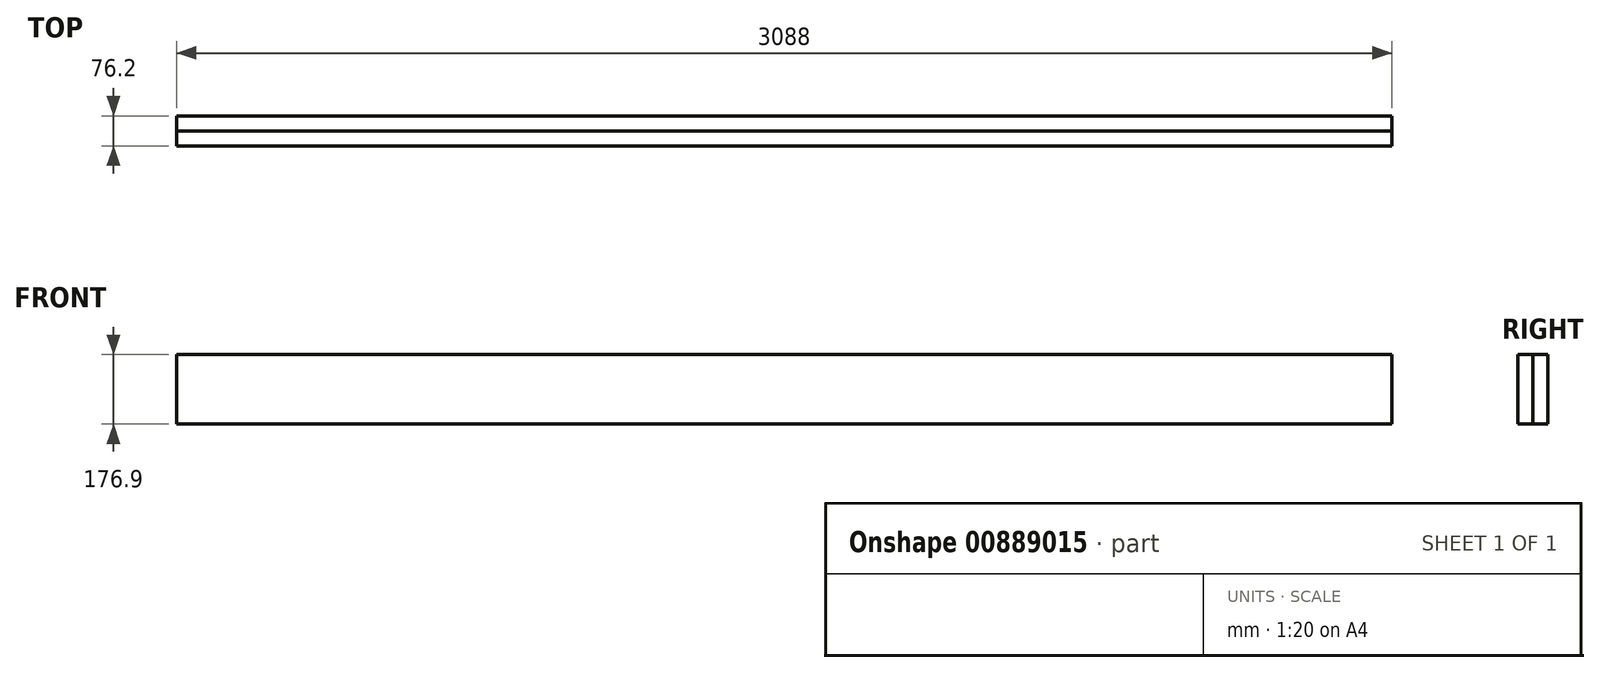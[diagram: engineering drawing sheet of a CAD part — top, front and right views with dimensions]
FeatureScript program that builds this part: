
annotation { "Feature Type Name" : "Feature", "Feature Type Description" : "" }
export const myFeature = defineFeature(function(context is Context, id is Id, definition is map)
    precondition{}
    {
        {
            var Q0;
            Q0=qCreatedBy(makeId("Top.planeOp"),FACE);
            var sketch = newSketch(context, id + "F0", { "sketchPlane" : qUnion([Q0])});
            skLineSegment(sketch, "E0.bottom", {"start": v(-1544, -38.1) * mm, "end": v(1544, -38.1) * mm});
            skLineSegment(sketch, "E0.top", {"start": v(-1544, 38.1) * mm, "end": v(1544, 38.1) * mm});
            skLineSegment(sketch, "E0.left", {"start": v(-1544, -38.1) * mm, "end": v(-1544, 38.1) * mm});
            skLineSegment(sketch, "E0.right", {"start": v(1544, -38.1) * mm, "end": v(1544, 38.1) * mm});
            skPoint(sketch, "E0.middle", {"position": v(0, 0) * mm});
            skLineSegment(sketch, "E1", {"start": v(-1544, 0) * mm, "end": v(1544, 0) * mm});
            skSolve(sketch);
        }
        {
            var Q0;
            {var subQ0=sQuery(id+"F0.wireOp",EDGE,"E0.top");Q0=makeQuery(id+"F0.imprint","IMPRINT",FACE,{"disambiguationData":[TD([[makeQuery(id+"F0.imprint","IMPRINT",EDGE,{"derivedFrom":subQ0}),-1.0]])]});}
            extrude(context, id + "F1", {"entities" : qUnion([Q0]), "endBound" : BoundingType.SYMMETRIC, "depth" : 176.9 * mm, "offsetDistance" : 25 * mm});
        }
        {
            var Q0;
            {var subQ0=sQuery(id+"F0.wireOp",EDGE,"E0.bottom");Q0=makeQuery(id+"F0.imprint","IMPRINT",FACE,{"disambiguationData":[TD([[makeQuery(id+"F0.imprint","IMPRINT",EDGE,{"derivedFrom":subQ0}),1.0]])]});}
            extrude(context, id + "F2", {"entities" : qUnion([Q0]), "endBound" : BoundingType.SYMMETRIC, "depth" : 176.9 * mm, "offsetDistance" : 25 * mm});
        }
    });
